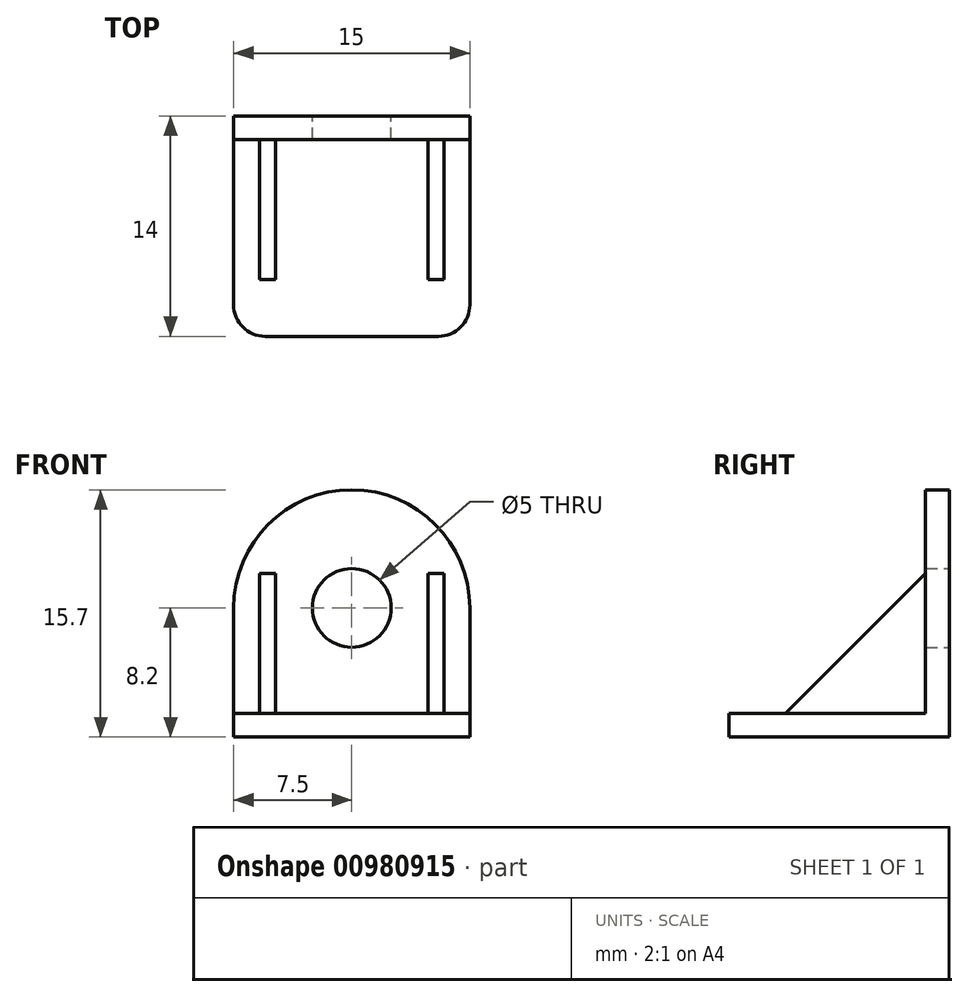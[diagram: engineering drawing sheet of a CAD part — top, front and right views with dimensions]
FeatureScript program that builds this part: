
annotation { "Feature Type Name" : "Feature", "Feature Type Description" : "" }
export const myFeature = defineFeature(function(context is Context, id is Id, definition is map)
    precondition{}
    {
        {
            var Q0;
            Q0=qCreatedBy(makeId("Front.planeOp"),FACE);
            var sketch = newSketch(context, id + "F0", { "sketchPlane" : qUnion([Q0])});
            skArc(sketch, "E0", {"start": v(7.5, 8.2) * mm, "mid": v(0, 15.7) * mm, "end": v(-7.5, 8.2) * mm});
            skLineSegment(sketch, "E1.bottom", {"start": v(-7.5, 0) * mm, "end": v(7.5, 0) * mm});
            skLineSegment(sketch, "E1.left", {"start": v(-7.5, 0) * mm, "end": v(-7.5, 8.2) * mm});
            skLineSegment(sketch, "E1.right", {"start": v(7.5, 0) * mm, "end": v(7.5, 8.2) * mm});
            skLineSegment(sketch, "E2", {"start": v(-21.93, 15.7) * mm, "end": v(21.5, 15.7) * mm, "construction": true});
            skCircle(sketch, "E3", {"center": v(0, 8.2) * mm, "radius": 2.5 * mm});
            skSolve(sketch);
        }
        {
            var Q0;
            Q0 = qSketchRegion(id + "F0", true);
            extrude(context, id + "F1", {"entities" : qUnion([Q0]), "depth" : 14 * mm, "offsetDistance" : 25 * mm});
        }
        {
            var Q0;
            Q0=qCreatedBy(makeId("Right.planeOp"),FACE);
            var sketch = newSketch(context, id + "F2", { "sketchPlane" : qUnion([Q0])});
            skLineSegment(sketch, "E4.bottom", {"start": v(-14, 18.43) * mm, "end": v(-1.5, 18.43) * mm});
            skLineSegment(sketch, "E4.top", {"start": v(-14, 1.5) * mm, "end": v(-1.5, 1.5) * mm});
            skLineSegment(sketch, "E4.left", {"start": v(-14, 18.43) * mm, "end": v(-14, 1.5) * mm});
            skLineSegment(sketch, "E4.right", {"start": v(-1.5, 18.43) * mm, "end": v(-1.5, 1.5) * mm});
            skSolve(sketch);
        }
        {
            var Q0;
            Q0 = qSketchRegion(id + "F2", true);
            extrude(context, id + "F3", {"entities" : qUnion([Q0]), "operationType" : NewBodyOperationType.REMOVE, "endBound" : BoundingType.SYMMETRIC, "oppositeDirection" : true, "depth" : 40 * mm, "offsetDistance" : 25 * mm});
        }
        {
            var Q0;
            Q0=qCreatedBy(makeId("Right.planeOp"),FACE);
            var sketch = newSketch(context, id + "F4", { "sketchPlane" : qUnion([Q0])});
            skLineSegment(sketch, "E5", {"start": v(-1.5, 10.4) * mm, "end": v(-10.4, 1.5) * mm});
            skLineSegment(sketch, "E6", {"start": v(-10.4, 1.5) * mm, "end": v(-1.5, 1.5) * mm});
            skLineSegment(sketch, "E7", {"start": v(-1.5, 1.5) * mm, "end": v(-1.5, 10.4) * mm});
            skSolve(sketch);
        }
        {
            var Q0;
            Q0 = qSketchRegion(id + "F4", true);
            extrude(context, id + "F5", {"entities" : qUnion([Q0]), "operationType" : NewBodyOperationType.ADD, "endBound" : BoundingType.SYMMETRIC, "depth" : 11.7 * mm, "offsetDistance" : 25 * mm});
        }
        {
            var Q0;
            Q0=makeQuery(id+"F3.boolean.opBoolean","COPY",FACE,{"derivedFrom":makeQuery(id+"F3.opExtrude","SWEPT_FACE",FACE,{"disambiguationData":[OSD([sQuery(id+"F2.wireOp",EDGE,"E4.top")])]})});
            var sketch = newSketch(context, id + "F6", { "sketchPlane" : qUnion([Q0])});
            skLineSegment(sketch, "E8.bottom", {"start": v(-4.85, -1.5) * mm, "end": v(4.85, -1.5) * mm});
            skLineSegment(sketch, "E8.top", {"start": v(-4.85, -15) * mm, "end": v(4.85, -15) * mm});
            skLineSegment(sketch, "E8.left", {"start": v(-4.85, -1.5) * mm, "end": v(-4.85, -15) * mm});
            skLineSegment(sketch, "E8.right", {"start": v(4.85, -1.5) * mm, "end": v(4.85, -15) * mm});
            skPoint(sketch, "E8.middle", {"position": v(0, -8.25) * mm});
            skSolve(sketch);
        }
        {
            var Q0;
            Q0 = qSketchRegion(id + "F6", true);
            extrude(context, id + "F7", {"entities" : qUnion([Q0]), "operationType" : NewBodyOperationType.REMOVE, "depth" : 26.2 * mm, "offsetDistance" : 25 * mm});
        }
        {
            var Q0;
            Q0=makeQuery(id+"F1.opExtrude","CAP_EDGE",EDGE,{"disambiguationData":[OSD([sQuery(id+"F0.wireOp",EDGE,"E1.right")])],"isStart":false});
            var Q1;
            Q1=makeQuery(id+"F1.opExtrude","CAP_EDGE",EDGE,{"disambiguationData":[OSD([sQuery(id+"F0.wireOp",EDGE,"E1.left")])],"isStart":false});
            fillet(context, id + "F8", {"entities" : qUnion([Q0, Q1]), "radius" : 2 * mm, "tangentPropagation" : true, "allowEdgeOverflow" : false});
        }
    });
